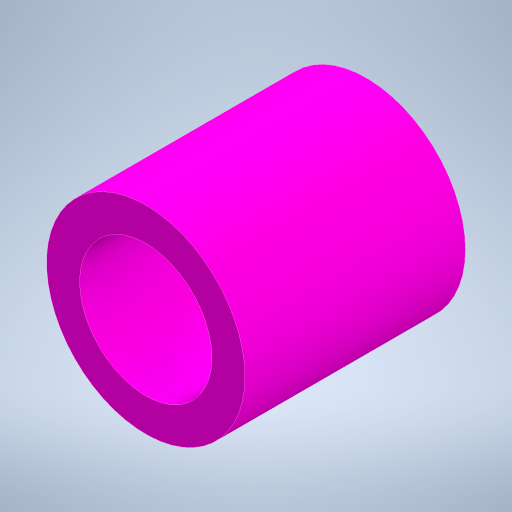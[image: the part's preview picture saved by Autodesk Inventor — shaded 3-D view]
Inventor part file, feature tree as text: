
AUTODESK INVENTOR PART (.ipt)
format: ipt  version: 2024 (Build 280153000, 153)  size: 206,848 bytes
history: native  units: in
note: dims shown in document units (in); Inventor stores cm internally (conversion verified against a paired STEP export)
features: extrude x2, sketch x1
ambient origin geometry x8: Origin, YZ Plane, XZ Plane, XY Plane, X Axis, Y Axis, Z Axis, Center Point
bodies: Solid1 (feature_tree)
feature tree (3):
  sketch  "Sketch1"  dims[d0=0.2362in d1=0.3543in d2=0.0394in d3=0.0in d4=0.3937in d5=0.0in]
  extrude  "Extrusion1"  Depth=0.3543in
  extrude  "Extrusion2"  Depth=0.0394in TaperAngle=0.0deg
